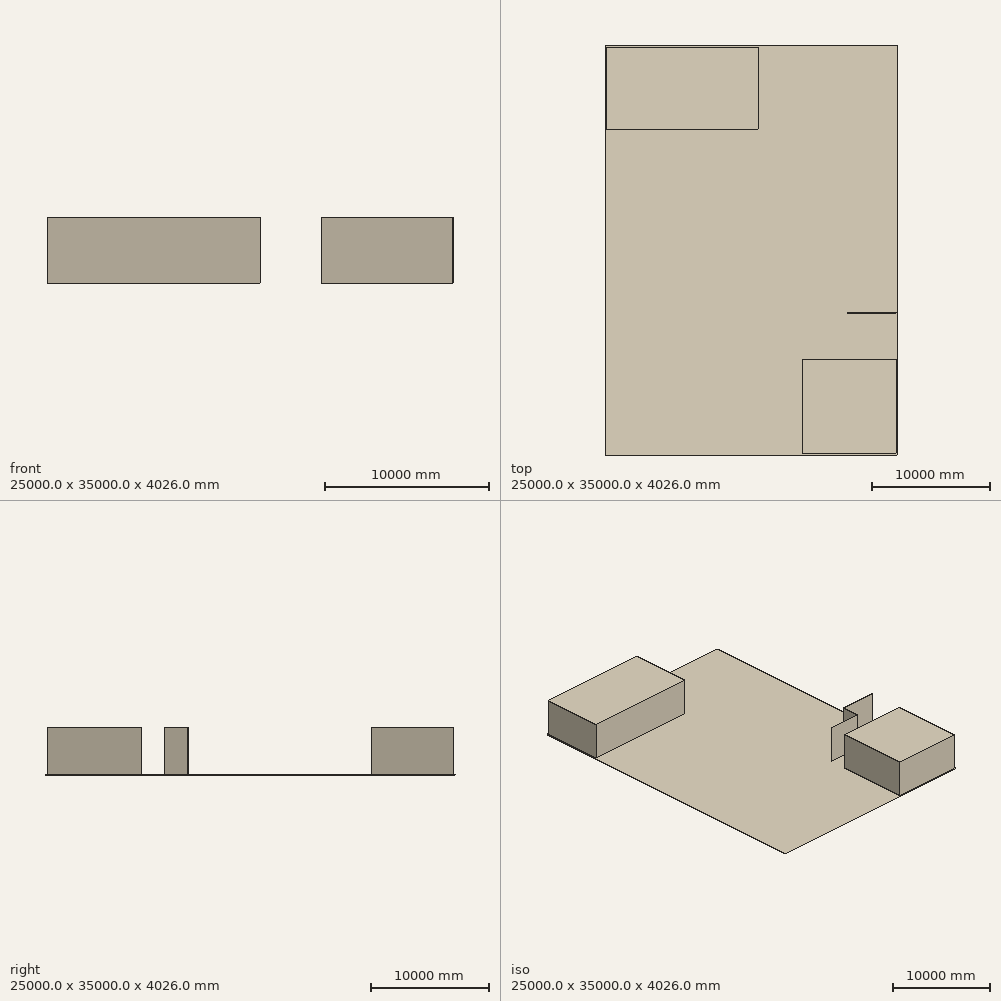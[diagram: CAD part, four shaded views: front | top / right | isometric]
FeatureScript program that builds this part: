
annotation { "Feature Type Name" : "Feature", "Feature Type Description" : "" }
export const myFeature = defineFeature(function(context is Context, id is Id, definition is map)
    precondition{}
    {
        {
            var Q0;
            Q0=qCreatedBy(makeId("Top.planeOp"),FACE);
            cPlane(context, id + "F0", {"entities" : qUnion([Q0]), "cplaneType" : CPlaneType.OFFSET, "offset" : 1 * mm, "width" : 150 * mm, "height" : 150 * mm});
        }
        {
            var Q0;
            Q0=qCreatedBy(makeId("Top.planeOp"),FACE);
            var sketch = newSketch(context, id + "F1", { "sketchPlane" : qUnion([Q0])});
            skLineSegment(sketch, "E0.bottom", {"start": v(12500, 17500) * mm, "end": v(-12500, 17500) * mm});
            skLineSegment(sketch, "E0.top", {"start": v(12500, -17500) * mm, "end": v(-12500, -17500) * mm});
            skLineSegment(sketch, "E0.left", {"start": v(12500, 17500) * mm, "end": v(12500, -17500) * mm});
            skLineSegment(sketch, "E0.right", {"start": v(-12500, 17500) * mm, "end": v(-12500, -17500) * mm});
            skPoint(sketch, "E0.middle", {"position": v(0, 0) * mm});
            skSolve(sketch);
        }
        {
            var Q0;
            Q0=qCreatedBy(id+"F0.planeOp",FACE);
            var sketch = newSketch(context, id + "F2", { "sketchPlane" : qUnion([Q0])});
            skLineSegment(sketch, "E1.bottom", {"start": v(-12369.59, 17370.87) * mm, "end": v(630.41, 17370.87) * mm});
            skLineSegment(sketch, "E1.top", {"start": v(-12369.59, 10370.87) * mm, "end": v(630.41, 10370.87) * mm});
            skLineSegment(sketch, "E1.left", {"start": v(-12369.59, 17370.87) * mm, "end": v(-12369.59, 10370.87) * mm});
            skLineSegment(sketch, "E1.right", {"start": v(630.41, 17370.87) * mm, "end": v(630.41, 10370.87) * mm});
            skLineSegment(sketch, "E2.bottom", {"start": v(12344.07, -17335.93) * mm, "end": v(4344.07, -17335.93) * mm});
            skLineSegment(sketch, "E2.top", {"start": v(12344.07, -9335.93) * mm, "end": v(4344.07, -9335.93) * mm});
            skLineSegment(sketch, "E2.left", {"start": v(12344.07, -17335.93) * mm, "end": v(12344.07, -9335.93) * mm});
            skLineSegment(sketch, "E2.right", {"start": v(4344.07, -17335.93) * mm, "end": v(4344.07, -9335.93) * mm});
            skLineSegment(sketch, "E3", {"start": v(4353.62, -7335.93) * mm, "end": v(8192.26, -7335.93) * mm});
            skLineSegment(sketch, "E4", {"start": v(8192.26, -7335.93) * mm, "end": v(8192.26, -5335.93) * mm});
            skLineSegment(sketch, "E5", {"start": v(8192.26, -5335.93) * mm, "end": v(12353.62, -5335.93) * mm});
            skLineSegment(sketch, "E6", {"start": v(12353.62, -5335.93) * mm, "end": v(12353.62, -5310.93) * mm});
            skLineSegment(sketch, "E7", {"start": v(12353.62, -5310.93) * mm, "end": v(8167.26, -5310.93) * mm});
            skLineSegment(sketch, "E8", {"start": v(8167.26, -5310.93) * mm, "end": v(8167.26, -7310.93) * mm});
            skLineSegment(sketch, "E9", {"start": v(8167.26, -7310.93) * mm, "end": v(4354.22, -7310.93) * mm});
            skLineSegment(sketch, "E10", {"start": v(4354.22, -7310.93) * mm, "end": v(4353.62, -7335.93) * mm});
            skSolve(sketch);
        }
        {
            var Q0;
            Q0 = qSketchRegion(id + "F1", true);
            extrude(context, id + "F3", {"entities" : qUnion([Q0]), "oppositeDirection" : true, "depth" : 25 * mm, "offsetDistance" : 25 * mm});
        }
        {
            var Q0;
            Q0 = qSketchRegion(id + "F2", true);
            extrude(context, id + "F4", {"entities" : qUnion([Q0]), "operationType" : NewBodyOperationType.ADD, "depth" : 4000 * mm, "offsetDistance" : 25 * mm});
        }
    });
